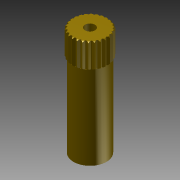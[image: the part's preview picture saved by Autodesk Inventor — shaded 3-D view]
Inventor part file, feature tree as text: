
AUTODESK INVENTOR PART (.ipt)
format: ipt  version: 2015 (Build 190159000, 159)  size: 349,696 bytes
history: native  units: in
note: dims shown in document units (in); Inventor stores cm internally (conversion verified against a paired STEP export)
features: mirror x1, other x1, imported_body x1
ambient origin geometry x8: Origin, YZ Plane, XZ Plane, XY Plane, X Axis, Y Axis, Z Axis, Center Point
bodies: Body1 (feature_tree)
feature tree (3):
  mirror  "Mirror1"
  other  "TOWER PRO MG-995, ANALOG SERVO, SHAFT.ipt1"
  imported_body  "Base1"
